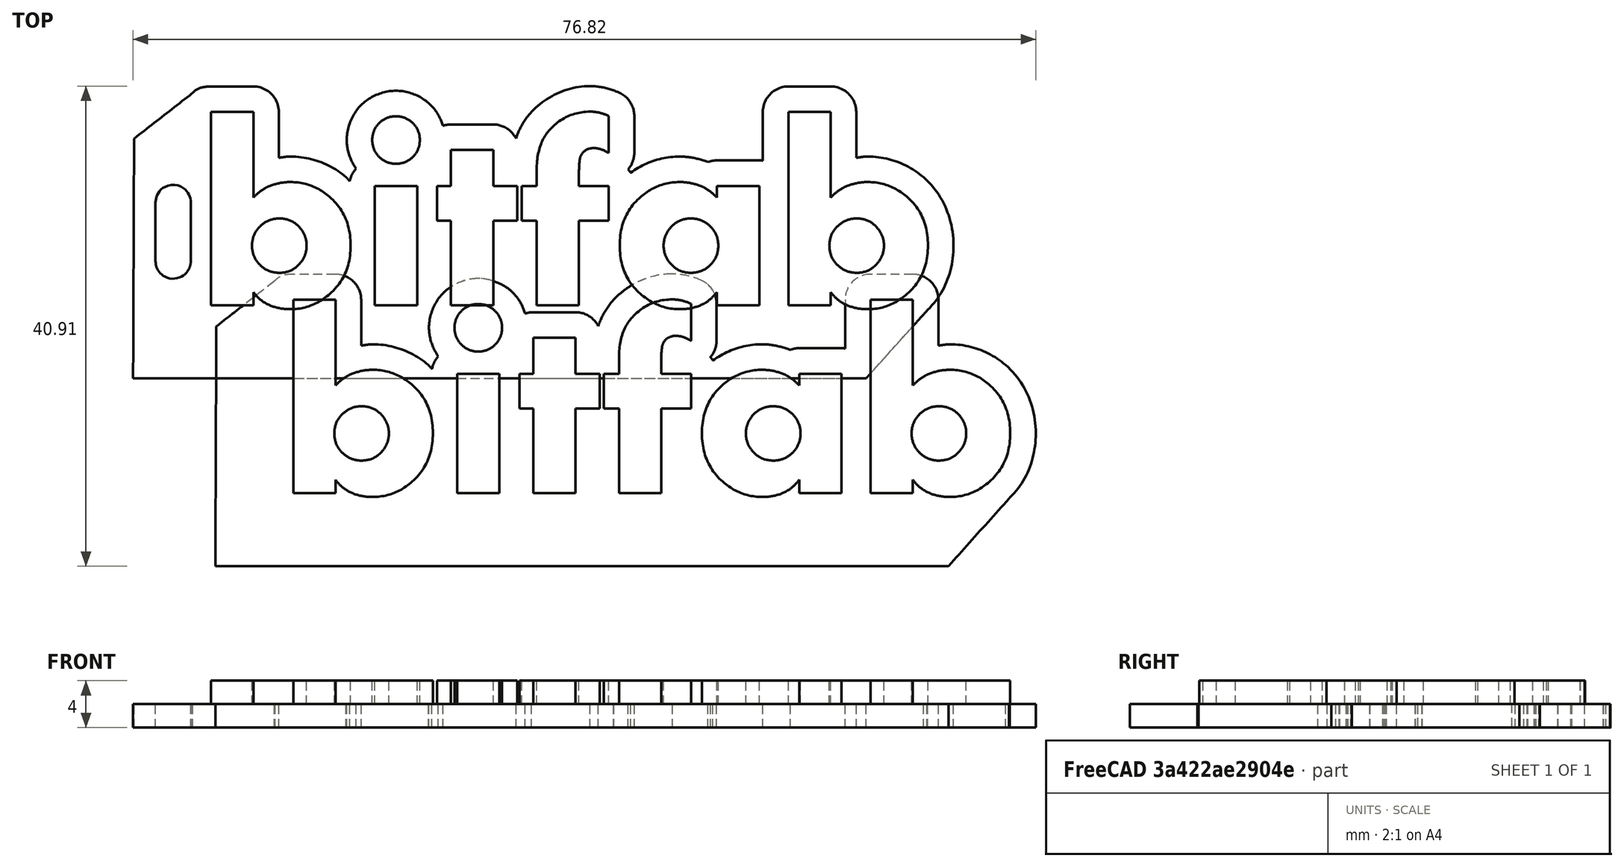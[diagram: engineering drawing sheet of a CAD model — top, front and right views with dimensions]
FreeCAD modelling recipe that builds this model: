
FCSTD DOCUMENT  (FreeCAD 0.16R6706 (Git))
Label: bitfab_keychain_logo
License: All rights reserved
LicenseURL: http://en.wikipedia.org/wiki/All_rights_reserved
objects: Part::Feature×13, Part::Extrusion×11, Part::MultiFuse×3, Part::Cut×2, Sketcher::SketchObject×2, Part::FeaturePython×1, PartDesign::Pad×1, Mesh::Feature×1
note: 34 computed .brp shape members not serialized (recipe doc carries the construction recipe); baked Part::Feature solids carry a one-line shape summary decoded from their .brp

FEATURE [Part::Feature] path4724
  shape: bbox 199.5 x 71.16 x 1.826e-06 mm, 0 faces, 0 solids (baked)
FEATURE [Part::Feature] path4146
  shape: bbox 33.94 x 48 x 1.826e-06 mm, 0 faces, 0 solids (baked)
FEATURE [Part::Feature] path4146001
  shape: bbox 13.29 x 13.22 x 1.826e-06 mm, 0 faces, 0 solids (baked)
FEATURE [Part::Feature] path4148
  shape: bbox 11.56 x 11.56 x 1.826e-06 mm, 0 faces, 0 solids (baked)
FEATURE [Part::Feature] path4148001
  shape: bbox 10.28 x 29.08 x 1.826e-06 mm, 0 faces, 0 solids (baked)
FEATURE [Part::Feature] path4150
  shape: bbox 19.52 x 37.82 x 1.826e-06 mm, 0 faces, 0 solids (baked)
FEATURE [Part::Feature] path4152
  shape: bbox 21.18 x 47.16 x 1.826e-06 mm, 0 faces, 0 solids (baked)
FEATURE [Part::Feature] path4154
  shape: bbox 33.94 x 30.96 x 1.826e-06 mm, 0 faces, 0 solids (baked)
FEATURE [Part::Feature] path4154001
  shape: bbox 13.29 x 13.22 x 1.826e-06 mm, 0 faces, 0 solids (baked)
FEATURE [Part::Feature] path4156
  shape: bbox 33.94 x 48 x 1.826e-06 mm, 0 faces, 0 solids (baked)
FEATURE [Part::Feature] path4156001
  shape: bbox 13.29 x 13.22 x 1.826e-06 mm, 0 faces, 0 solids (baked)
FEATURE [Part::Extrusion] Extrude
  Base = -> path4146
  Dir = (0,0,8)
  Solid = true
FEATURE [Part::Extrusion] Extrude001
  Base = -> path4148
  Dir = (0,0,8)
  Solid = true
FEATURE [Part::Extrusion] Extrude002
  Base = -> path4148001
  Dir = (0,0,8)
  Solid = true
FEATURE [Part::Extrusion] Extrude003
  Base = -> path4150
  Dir = (0,0,8)
  Solid = true
FEATURE [Part::Extrusion] Extrude004
  Base = -> path4152
  Dir = (0,0,8)
  Solid = true
FEATURE [Part::Extrusion] Extrude005
  Base = -> path4154
  Dir = (0,0,8)
  Solid = true
FEATURE [Part::Extrusion] Extrude006
  Base = -> path4156
  Dir = (0,0,8)
  Solid = true
FEATURE [Part::Extrusion] Extrude007
  Base = -> path4146001
  Dir = (0,0,8)
  Solid = true
FEATURE [Part::Extrusion] Extrude008
  Base = -> path4154001
  Dir = (0,0,8)
  Solid = true
FEATURE [Part::Extrusion] Extrude009
  Base = -> path4156001
  Dir = (0,0,8)
  Solid = true
FEATURE [Part::MultiFuse] Fusion  label="letters"
  Shapes = -> [Extrude,Extrude003,Extrude002,Extrude001,Extrude006,Extrude004,Extrude005]
FEATURE [Part::MultiFuse] Fusion001  label="holes"
  Shapes = -> [Extrude007,Extrude009,Extrude008]
FEATURE [Part::Extrusion] Extrude010  label="outline"
  Base = -> path4724
  Dir = (0,0,4)
  Solid = true
FEATURE [Part::Cut] Cut
  Base = -> Fusion
  Tool = -> Fusion001
FEATURE [Part::MultiFuse] Fusion002
  Shapes = -> [Extrude010,Cut]
FEATURE [Part::FeaturePython] Clone  label="Clone of Fusion002"  # Draft clone (typed FeaturePython)
  Objects = -> [Fusion002]
  Placement = pos=(-7,16,0) rot=(0,0,1;0rad)
  Scale = (0.35,0.35,0.5)
FEATURE [Sketcher::SketchObject] Sketch
  sketch-geometry (4):
    g0: LineSegment StartX=0 StartY=0 StartZ=0 EndX=65 EndY=0 EndZ=0
    g1: LineSegment StartX=65 StartY=0 StartZ=0 EndX=65 EndY=-21.8082 EndZ=0
    g2: LineSegment StartX=65 StartY=-21.8082 StartZ=0 EndX=0 EndY=-21.8082 EndZ=0
    g3: LineSegment StartX=0 StartY=-21.8082 StartZ=0 EndX=0 EndY=0 EndZ=0
  constraints (10):
    c: Coincident(g0,g1)
    c: Coincident(g1,g2)
    c: Coincident(g2,g3)
    c: Coincident(g3,g0)
    c: Horizontal(g0)
    c: Horizontal(g2)
    c: Vertical(g1)
    c: Vertical(g3)
    c: Coincident(g0,g-1)
    c: DistanceX(g0,g0) = 65
FEATURE [Part::Feature] Clone001  label="Clone of Fusion003"
  shape: bbox 69.82 x 24.9 x 4 mm, 175 faces (baked)
FEATURE [Sketcher::SketchObject] Sketch001
  sketch-geometry (4):
    g0: ArcOfCircle CenterX=0 CenterY=2.5 CenterZ=0 NormalX=0 NormalY=0 NormalZ=1 Radius=1.5 StartAngle=0 EndAngle=3.14159
    g1: ArcOfCircle CenterX=0 CenterY=-2.5 CenterZ=0 NormalX=0 NormalY=0 NormalZ=1 Radius=1.5 StartAngle=3.14159 EndAngle=6.28319
    g2: LineSegment StartX=-1.5 StartY=2.5 StartZ=0 EndX=-1.5 EndY=-2.5 EndZ=0
    g3: LineSegment StartX=1.5 StartY=2.5 StartZ=0 EndX=1.5 EndY=-2.5 EndZ=0
  constraints (9):
    c: Tangent(g0,g3) = 1.5708
    c: Tangent(g0,g2) = -1.5708
    c: Tangent(g2,g1) = -1.5708
    c: Tangent(g3,g1) = 1.5708
    c: Vertical(g2)
    c: Equal(g0,g1)
    c: Symmetric(g0,g1,g-1)
    c: DistanceY(g1,g0) = 5
    c: DistanceX(g0,g0) = 3
FEATURE [PartDesign::Pad] Pad  label="agujero llaves"
  Length = 10
  Length2 = 100
  Midplane = true
  Sketch = -> Sketch001
  Type = 0
FEATURE [Part::Feature] Clone_solid  label="Clone of Fusion002 (Solid)"
  shape: bbox 69.82 x 24.9 x 4 mm, 175 faces (baked)
FEATURE [Part::Cut] Cut001
  Base = -> Clone_solid
  Tool = -> Pad
FEATURE [Mesh::Feature] Mesh001  label="Cut001 (Meshed)"
